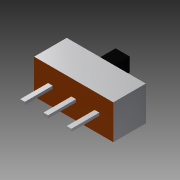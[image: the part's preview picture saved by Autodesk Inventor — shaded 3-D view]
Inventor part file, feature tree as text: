
AUTODESK INVENTOR PART (.ipt)
format: ipt  version: 2014 SP1 (Build 180222100, 222)  size: 128,512 bytes
history: native  units: mm
features: extrude x4, sketch x4, chamfer x1
ambient origin geometry x8: Origin, YZ Plane, XZ Plane, XY Plane, X Axis, Y Axis, Z Axis, Center Point
bodies: Solid1 (feature_tree)
feature tree (9):
  extrude  "Extrusion1"  Depth=3.7mm
  extrude  "Extrusion2"  Depth=0.5mm
  extrude  "Extrusion3"  Depth=2.5mm
  extrude  "Extrusion4"  Depth=3.0mm TaperAngle=0.0deg
  chamfer  "Chamfer1"  Distance=1.6mm
  sketch  "Sketch1"  dims[d0=8.5mm d1=3.7mm]
  sketch  "Sketch2"  dims[d2=3.5mm d3=0.0mm d4=0.5mm]
  sketch  "Sketch3"  dims[d5=0.3mm d6=2.5mm]
  sketch  "Sketch4"  dims[d7=30.0mm d9=2.5mm d10=10.0mm d12=10.0mm d14=3.0mm d15=0.0mm d16=1.6mm d17=3.6mm d18=0.5mm d19=0.0mm d20=1.5mm d21=0.05mm d22=3.5mm d23=0.0mm d24=0.25mm d25=2.0mm d26=45.0deg]
